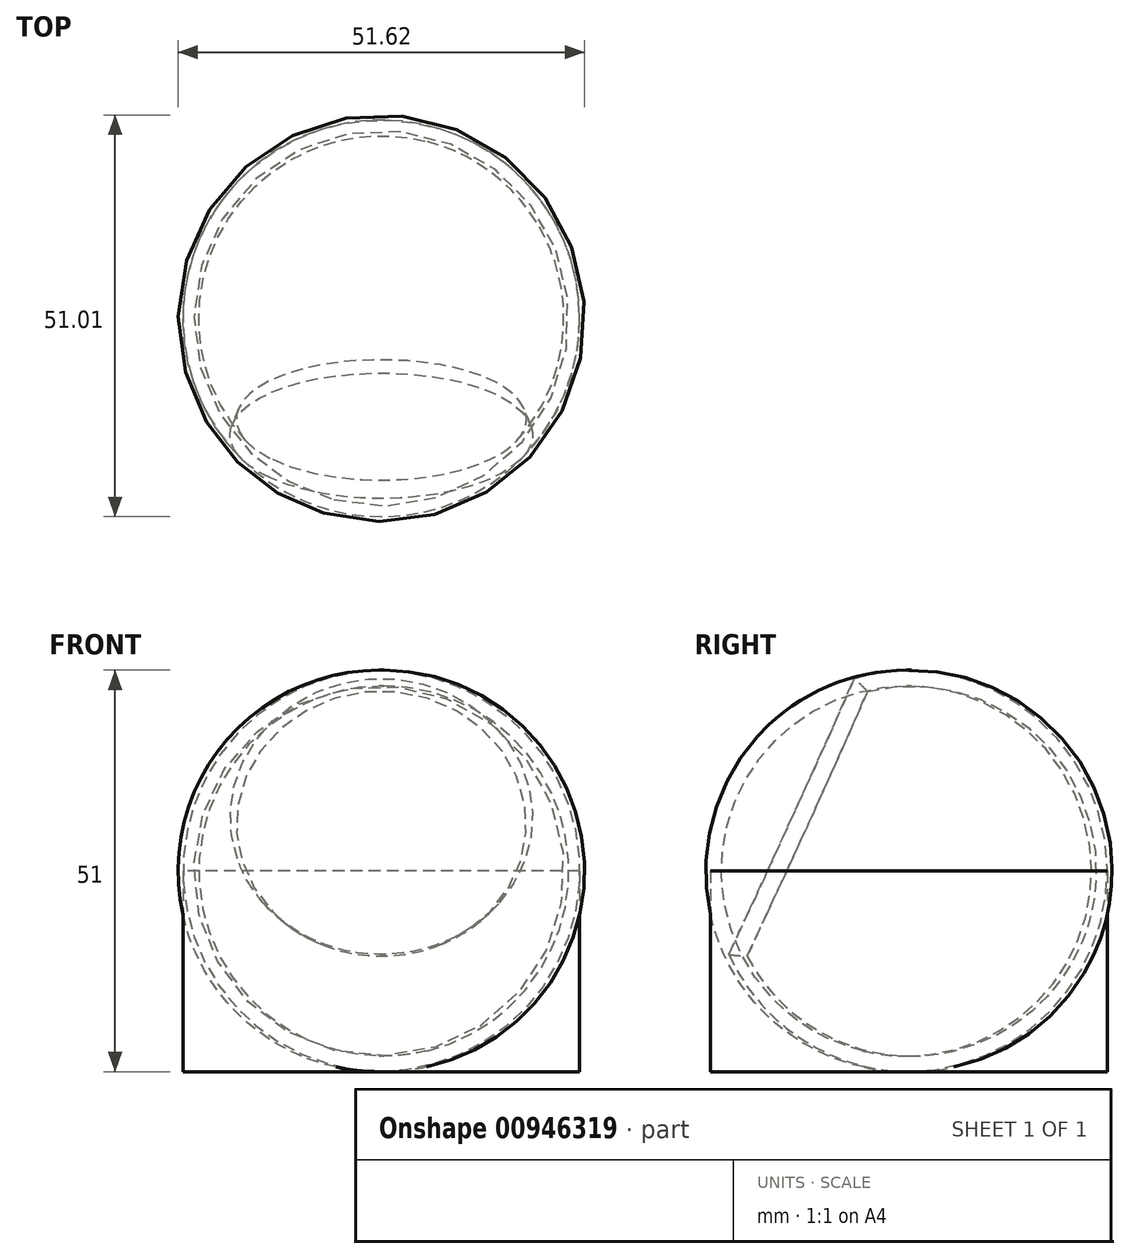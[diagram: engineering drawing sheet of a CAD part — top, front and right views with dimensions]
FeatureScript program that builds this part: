
annotation { "Feature Type Name" : "Feature", "Feature Type Description" : "" }
export const myFeature = defineFeature(function(context is Context, id is Id, definition is map)
    precondition{}
    {
        {
            assignVariable(context, id + "F0", {"name" : "holderDim", "anyValue" : 49});
        }
        {
            var Q0;
            Q0=qCreatedBy(makeId("Front.planeOp"),FACE);
            var sketch = newSketch(context, id + "F1", { "sketchPlane" : qUnion([Q0])});
            skCircle(sketch, "E0", {"center": v(-0.31, 25.5) * mm, "radius": 25.5 * mm});
            skLineSegment(sketch, "E1", {"start": v(0, 51) * mm, "end": v(0, 0) * mm});
            skCircle(sketch, "E2.0", {"center": v(-0.31, 25.5) * mm, "radius": 23.5 * mm});
            skSolve(sketch);
        }
        {
            var Q0;
            {var subQ0=sQuery(id+"F1.wireOp",EDGE,"E1");Q0=makeQuery(id+"F1.imprint","IMPRINT",FACE,{"disambiguationData":[TD([[makeQuery(id+"F1.imprint","IMPRINT",EDGE,{"derivedFrom":subQ0}),1.0]])]});}
            var Q1;
            {var subQ0=sQuery(id+"F1.wireOp",EDGE,"E2.0");var subQ1=sQuery(id+"F1.wireOp",EDGE,"E1");var subQ2=makeQuery(id+"F1.imprint","INTERSECT",VERTEX,{"disambiguationData":[OD(0.0)],"derivedFrom":[subQ1,subQ0]});Q1=makeQuery(id+"F1.imprint","IMPRINT",FACE,{"disambiguationData":[TD([[makeQuery(id+"F1.imprint","IMPRINT",EDGE,{"disambiguationData":[TD([[subQ2,-1.0]])],"derivedFrom":subQ1}),1.0]])]});}
            var Q2;
            Q2=sQuery(id+"F1.wireOp",EDGE,"E1");
            revolve(context, id + "F2", {"surfaceOperationType" : NewSurfaceOperationType.NEW, "entities" : qUnion([Q0, Q1]), "axis" : qUnion([Q2]), "revolveType" : RevolveType.FULL});
        }
        {
            var Q0;
            {var subQ0=sQuery(id+"F1.wireOp",EDGE,"E2.0");var subQ1=sQuery(id+"F1.wireOp",EDGE,"E1");var subQ2=makeQuery(id+"F1.imprint","INTERSECT",VERTEX,{"disambiguationData":[OD(0.0)],"derivedFrom":[subQ1,subQ0]});Q0=makeQuery(id+"F1.imprint","IMPRINT",FACE,{"disambiguationData":[TD([[makeQuery(id+"F1.imprint","IMPRINT",EDGE,{"disambiguationData":[TD([[subQ2,-1.0]])],"derivedFrom":subQ1}),1.0]])]});}
            var Q1;
            Q1=sQuery(id+"F1.wireOp",EDGE,"E1");
            revolve(context, id + "F3", {"surfaceOperationType" : NewSurfaceOperationType.NEW, "entities" : qUnion([Q0]), "axis" : qUnion([Q1]), "revolveType" : RevolveType.FULL});
        }
        {
            var Q0;
            Q0=qCreatedBy(makeId("Top.planeOp"),FACE);
            var sketch = newSketch(context, id + "F4", { "sketchPlane" : qUnion([Q0])});
            skCircle(sketch, "E3", {"center": v(0, 0) * mm, "radius": 25.2 * mm});
            skSolve(sketch);
        }
        {
            var Q0;
            Q0=sQuery(id+"F1.wireOp",EDGE,"E1");
            cPoint(context, id + "F5", {"entities" : qUnion([Q0]), "parameter" : 0.5});
        }
        {
            var Q0;
            Q0=qCreatedBy(makeId("Top.planeOp"),FACE);
            var Q1;
            Q1 = qCreatedBy(id + "F5" ,VERTEX);
            cPlane(context, id + "F6", {"entities" : qUnion([Q0, Q1]), "cplaneType" : CPlaneType.PLANE_POINT, "offset" : 25 * mm, "width" : 150 * mm, "height" : 150 * mm});
        }
        {
            var Q0;
            Q0 = qSketchRegion(id + "F4", true);
            var Q1;
            Q1=qCreatedBy(id+"F6.planeOp",FACE);
            extrude(context, id + "F7", {"entities" : qUnion([Q0]), "endBound" : BoundingType.UP_TO_SURFACE, "depth" : ((getVariable(context, 'holderDim') + 2) / 2) * mm, "endBoundEntityFace" : qUnion([Q1]), "offsetDistance" : 25 * mm});
        }
        {
            var Q0;
            Q0=qCreatedBy(makeId("Right.planeOp"),FACE);
            var sketch = newSketch(context, id + "F8", { "sketchPlane" : qUnion([Q0])});
            skCircle(sketch, "E4", {"center": v(-19.9, 34.67) * mm, "radius": 20 * mm});
            skLineSegment(sketch, "E5", {"start": v(-19.9, 54.67) * mm, "end": v(-19.9, 14.67) * mm});
            skSolve(sketch);
        }
        {
            var Q0;
            {var subQ0=sQuery(id+"F8.wireOp",EDGE,"E5");Q0=makeQuery(id+"F8.imprint","IMPRINT",FACE,{"disambiguationData":[TD([[makeQuery(id+"F8.imprint","IMPRINT",EDGE,{"derivedFrom":subQ0}),-1.0]])]});}
            var Q1;
            Q1=sQuery(id+"F8.wireOp",EDGE,"E5");
            revolve(context, id + "F9", {"surfaceOperationType" : NewSurfaceOperationType.NEW, "entities" : qUnion([Q0]), "axis" : qUnion([Q1]), "revolveType" : RevolveType.FULL});
        }
        {
            var Q0;
            Q0=makeQuery(id+"F9.opRevolve","SWEPT_BODY",BODY,{"disambiguationData":[OSD([sQuery(id+"F8.wireOp",EDGE,"E4"),sQuery(id+"F8.wireOp",EDGE,"E5")])]});
            var Q1;
            Q1=makeQuery(id+"F2.opRevolve","SWEPT_BODY",BODY,{"disambiguationData":[OSD([sQuery(id+"F1.wireOp",EDGE,"E0"),sQuery(id+"F1.wireOp",EDGE,"E1")])]});
            booleanBodies(context, id + "F10", {"operationType" : BooleanOperationType.SUBTRACTION, "tools" : qUnion([Q0]), "targets" : qUnion([Q1])});
        }
        {
            var Q0;
            Q0=makeQuery(id+"F3.opRevolve","SWEPT_BODY",BODY,{"disambiguationData":[OSD([sQuery(id+"F1.wireOp",EDGE,"E1"),sQuery(id+"F1.wireOp",EDGE,"E2.0")])]});
            var Q1;
            Q1=makeQuery(id+"F2.opRevolve","SWEPT_BODY",BODY,{"disambiguationData":[OSD([sQuery(id+"F1.wireOp",EDGE,"E0"),sQuery(id+"F1.wireOp",EDGE,"E1")])]});
            booleanBodies(context, id + "F11", {"operationType" : BooleanOperationType.SUBTRACTION, "tools" : qUnion([Q0]), "targets" : qUnion([Q1])});
        }
    });
